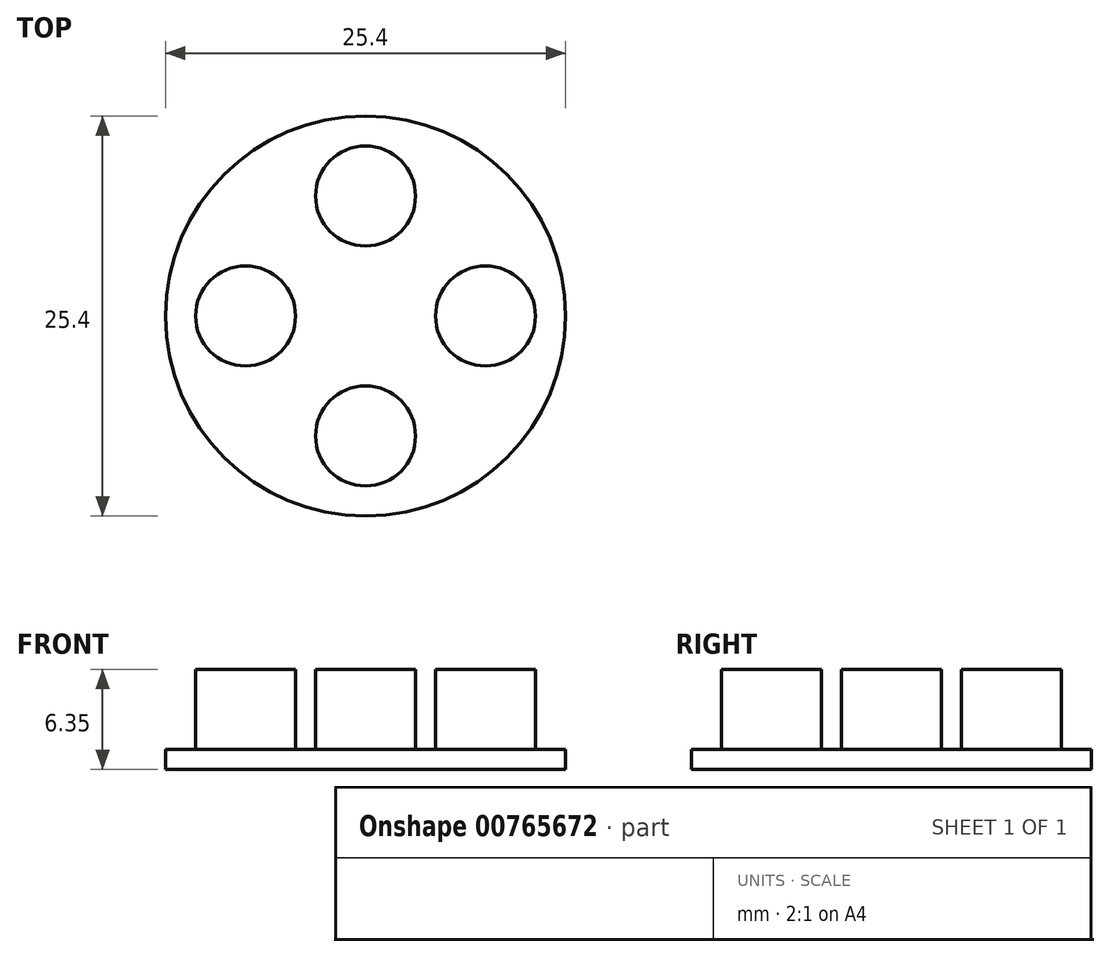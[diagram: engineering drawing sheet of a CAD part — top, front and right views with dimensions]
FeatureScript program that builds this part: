
annotation { "Feature Type Name" : "Feature", "Feature Type Description" : "" }
export const myFeature = defineFeature(function(context is Context, id is Id, definition is map)
    precondition{}
    {
        {
            var Q0;
            Q0=qCreatedBy(makeId("Top.planeOp"),FACE);
            var sketch = newSketch(context, id + "F0", { "sketchPlane" : qUnion([Q0])});
            skCircle(sketch, "E0", {"center": v(0, 0) * mm, "radius": 12.7 * mm});
            skSolve(sketch);
        }
        {
            var Q0;
            Q0=makeQuery(id+"F0.imprint","IMPRINT",FACE,{"disambiguationData":[TD([[makeQuery(id+"F0.imprint","IMPRINT",EDGE,{"derivedFrom":sQuery(id+"F0.wireOp",EDGE,"E0")}),1.0]])]});
            extrude(context, id + "F1", {"entities" : qUnion([Q0]), "depth" : 1.27 * mm, "offsetDistance" : 25.4 * mm});
        }
        {
            var Q0;
            Q0=qCreatedBy(makeId("Top.planeOp"),FACE);
            cPlane(context, id + "F2", {"entities" : qUnion([Q0]), "cplaneType" : CPlaneType.OFFSET, "offset" : 1.27 * mm, "width" : 152.4 * mm, "height" : 152.4 * mm});
        }
        {
            var Q0;
            Q0=qCreatedBy(id+"F2.planeOp",FACE);
            var sketch = newSketch(context, id + "F3", { "sketchPlane" : qUnion([Q0])});
            skCircle(sketch, "E1", {"center": v(0, 7.62) * mm, "radius": 3.18 * mm});
            skCircle(sketch, "E2", {"center": v(7.62, 0) * mm, "radius": 3.18 * mm});
            skCircle(sketch, "E3", {"center": v(0, -7.62) * mm, "radius": 3.18 * mm});
            skCircle(sketch, "E4", {"center": v(-7.62, 0) * mm, "radius": 3.18 * mm});
            skSolve(sketch);
        }
        {
            var Q0;
            Q0 = qSketchRegion(id + "F3", true);
            extrude(context, id + "F4", {"entities" : qUnion([Q0]), "operationType" : NewBodyOperationType.ADD, "depth" : 5.08 * mm, "offsetDistance" : 25.4 * mm});
        }
    });
